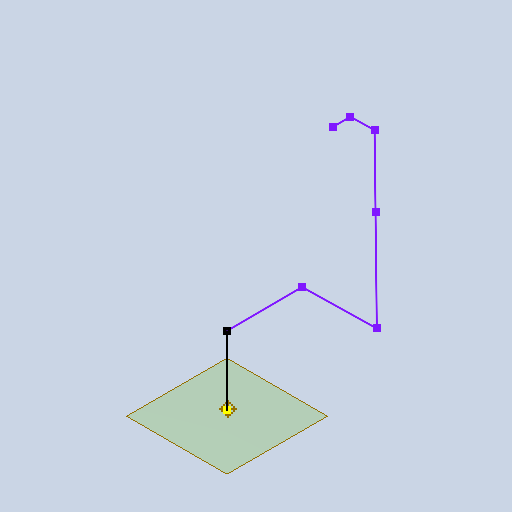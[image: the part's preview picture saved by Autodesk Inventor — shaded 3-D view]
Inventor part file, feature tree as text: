
AUTODESK INVENTOR PART (.ipt)
format: ipt  version: 2025 (Build 290162000, 162)  size: 168,960 bytes
history: native  units: in
note: dims shown in document units (in); Inventor stores cm internally (conversion verified against a paired STEP export)
features: other x1, plane x1, sketch x1
ambient origin geometry x8: Origin, YZ Plane, XZ Plane, XY Plane, X Axis, Y Axis, Z Axis, Center Point
feature tree (3):
  other  "Work Point1"
  plane  "Work Plane1"
  sketch  "3D Sketch1"
